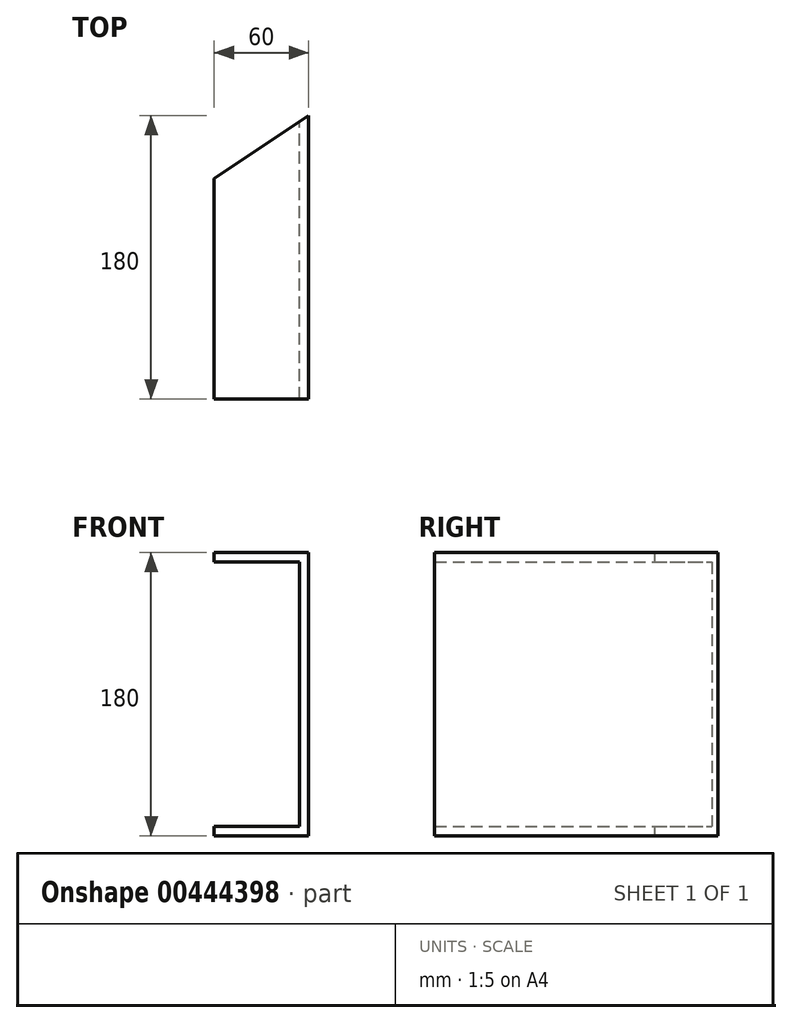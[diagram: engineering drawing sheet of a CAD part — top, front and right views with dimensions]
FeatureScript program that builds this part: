
annotation { "Feature Type Name" : "Feature", "Feature Type Description" : "" }
export const myFeature = defineFeature(function(context is Context, id is Id, definition is map)
    precondition{}
    {
        {
            var Q0;
            Q0=qCreatedBy(makeId("Front.planeOp"),FACE);
            var sketch = newSketch(context, id + "F0", { "sketchPlane" : qUnion([Q0])});
            skLineSegment(sketch, "E0.bottom", {"start": v(0, 180) * mm, "end": v(60, 180) * mm});
            skLineSegment(sketch, "E0.top", {"start": v(0, 0) * mm, "end": v(60, 0) * mm});
            skLineSegment(sketch, "E0.left", {"start": v(0, 180) * mm, "end": v(0, 174) * mm});
            skLineSegment(sketch, "E0.right", {"start": v(60, 180) * mm, "end": v(60, 0) * mm});
            skLineSegment(sketch, "E1.0", {"start": v(54, 174) * mm, "end": v(54, 6) * mm});
            skLineSegment(sketch, "E1.1", {"start": v(0, 174) * mm, "end": v(54, 174) * mm});
            skLineSegment(sketch, "E1.3", {"start": v(0, 6) * mm, "end": v(54, 6) * mm});
            skLineSegment(sketch, "E2.trimOffspring", {"start": v(0, 6) * mm, "end": v(0, 0) * mm});
            skSolve(sketch);
        }
        {
            var Q0;
            Q0 = qSketchRegion(id + "F0", true);
            extrude(context, id + "F1", {"entities" : qUnion([Q0]), "depth" : 180 * mm});
        }
        {
            var Q0;
            Q0=makeQuery(id+"F1.opExtrude","SWEPT_FACE",FACE,{"disambiguationData":[OSD([sQuery(id+"F0.wireOp",EDGE,"E0.bottom")])]});
            var sketch = newSketch(context, id + "F2", { "sketchPlane" : qUnion([Q0])});
            skLineSegment(sketch, "E3", {"start": v(0, 0) * mm, "end": v(0, -40) * mm});
            skLineSegment(sketch, "E4", {"start": v(0, -40) * mm, "end": v(60, 0) * mm});
            skLineSegment(sketch, "E5", {"start": v(60, 0) * mm, "end": v(0, 0) * mm});
            skSolve(sketch);
        }
        {
            var Q0;
            Q0 = qSketchRegion(id + "F2", true);
            extrude(context, id + "F3", {"entities" : qUnion([Q0]), "operationType" : NewBodyOperationType.REMOVE, "endBound" : BoundingType.THROUGH_ALL, "oppositeDirection" : true, "depth" : 25 * mm});
        }
    });
